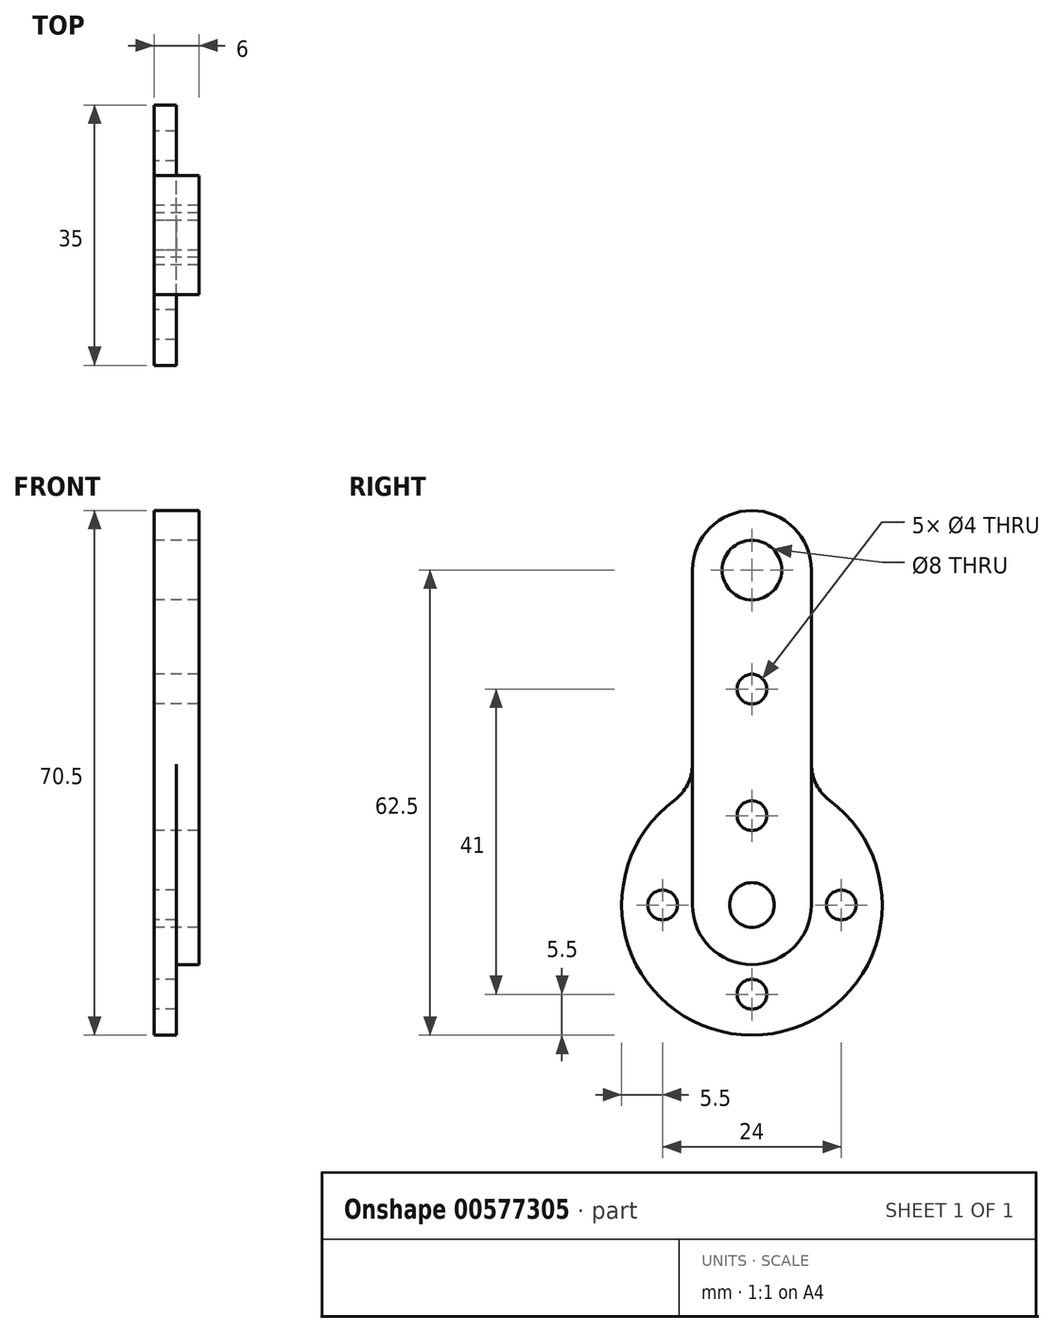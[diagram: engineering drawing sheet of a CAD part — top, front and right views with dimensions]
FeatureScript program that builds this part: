
annotation { "Feature Type Name" : "Feature", "Feature Type Description" : "" }
export const myFeature = defineFeature(function(context is Context, id is Id, definition is map)
    precondition{}
    {
        {
            var Q0;
            Q0=qCreatedBy(makeId("Right.planeOp"),FACE);
            var sketch = newSketch(context, id + "F0", { "sketchPlane" : qUnion([Q0])});
            skArc(sketch, "E0", {"start": v(-10.43, 14.06) * mm, "mid": v(0, -17.5) * mm, "end": v(10.43, 14.06) * mm});
            skCircle(sketch, "E1", {"center": v(0, 0) * mm, "radius": 3 * mm});
            skCircle(sketch, "E2", {"center": v(0, 12) * mm, "radius": 2 * mm});
            skCircle(sketch, "E3.1.0", {"center": v(-12, 0) * mm, "radius": 2 * mm});
            skCircle(sketch, "E3.2.0", {"center": v(0, -12) * mm, "radius": 2 * mm});
            skCircle(sketch, "E3.3.0", {"center": v(12, 0) * mm, "radius": 2 * mm});
            skLineSegment(sketch, "E4", {"start": v(8, 18.87) * mm, "end": v(8, 45) * mm});
            skLineSegment(sketch, "E5", {"start": v(-8, 18.87) * mm, "end": v(-8, 45) * mm});
            skArc(sketch, "E6", {"start": v(8, 45) * mm, "mid": v(0, 53) * mm, "end": v(-8, 45) * mm});
            skCircle(sketch, "E7", {"center": v(0, 45) * mm, "radius": 4 * mm});
            skPoint(sketch, "E8.visualSharp", {"position": v(-8, 15.56) * mm});
            skArc(sketch, "E8.filletArc", {"start": v(-10.43, 14.06) * mm, "mid": v(-8.64, 16.18) * mm, "end": v(-8, 18.87) * mm});
            skPoint(sketch, "E9.visualSharp", {"position": v(8, 15.56) * mm});
            skArc(sketch, "E9.filletArc", {"start": v(8, 18.87) * mm, "mid": v(8.64, 16.18) * mm, "end": v(10.43, 14.06) * mm});
            skSolve(sketch);
        }
        {
            var Q0;
            Q0 = qSketchRegion(id + "F0", true);
            extrude(context, id + "F1", {"entities" : qUnion([Q0]), "depth" : 6 * mm, "offsetDistance" : 25 * mm});
        }
        {
            var Q0;
            Q0=makeQuery(id+"F1.opExtrude","CAP_FACE",FACE,{"disambiguationData":[OSD([sQuery(id+"F0.wireOp",EDGE,"E0"),sQuery(id+"F0.wireOp",EDGE,"E1"),sQuery(id+"F0.wireOp",EDGE,"E2"),sQuery(id+"F0.wireOp",EDGE,"E3.1.0"),sQuery(id+"F0.wireOp",EDGE,"E3.2.0"),sQuery(id+"F0.wireOp",EDGE,"E3.3.0"),sQuery(id+"F0.wireOp",EDGE,"E4"),sQuery(id+"F0.wireOp",EDGE,"E5"),sQuery(id+"F0.wireOp",EDGE,"E6"),sQuery(id+"F0.wireOp",EDGE,"E7"),sQuery(id+"F0.wireOp",EDGE,"E8.filletArc"),sQuery(id+"F0.wireOp",EDGE,"E9.filletArc")])],"isStart":true});
            var sketch = newSketch(context, id + "F2", { "sketchPlane" : qUnion([Q0])});
            skCircle(sketch, "E10", {"center": v(0, 29) * mm, "radius": 2 * mm});
            skSolve(sketch);
        }
        {
            var Q0;
            Q0 = qSketchRegion(id + "F2", true);
            extrude(context, id + "F3", {"entities" : qUnion([Q0]), "operationType" : NewBodyOperationType.REMOVE, "endBound" : BoundingType.THROUGH_ALL, "oppositeDirection" : true, "depth" : 25 * mm, "offsetDistance" : 25 * mm});
        }
        {
            var Q0;
            Q0=makeQuery(id+"F1.opExtrude","CAP_FACE",FACE,{"disambiguationData":[OSD([sQuery(id+"F0.wireOp",EDGE,"E0"),sQuery(id+"F0.wireOp",EDGE,"E1"),sQuery(id+"F0.wireOp",EDGE,"E2"),sQuery(id+"F0.wireOp",EDGE,"E3.1.0"),sQuery(id+"F0.wireOp",EDGE,"E3.2.0"),sQuery(id+"F0.wireOp",EDGE,"E3.3.0"),sQuery(id+"F0.wireOp",EDGE,"E4"),sQuery(id+"F0.wireOp",EDGE,"E5"),sQuery(id+"F0.wireOp",EDGE,"E6"),sQuery(id+"F0.wireOp",EDGE,"E7"),sQuery(id+"F0.wireOp",EDGE,"E8.filletArc"),sQuery(id+"F0.wireOp",EDGE,"E9.filletArc")])],"isStart":false});
            var sketch = newSketch(context, id + "F4", { "sketchPlane" : qUnion([Q0])});
            skLineSegment(sketch, "E11", {"start": v(-8, 18.87) * mm, "end": v(-8, 0) * mm});
            skLineSegment(sketch, "E12", {"start": v(8, 18.87) * mm, "end": v(8, 0) * mm});
            skArc(sketch, "E13", {"start": v(-8, 0) * mm, "mid": v(0, -8) * mm, "end": v(8, 0) * mm});
            skArc(sketch, "E14", {"start": v(-8, 18.87) * mm, "mid": v(0, -20.5) * mm, "end": v(8, 18.87) * mm});
            skSolve(sketch);
        }
        {
            var Q0;
            Q0 = qSketchRegion(id + "F4", true);
            extrude(context, id + "F5", {"entities" : qUnion([Q0]), "operationType" : NewBodyOperationType.REMOVE, "oppositeDirection" : true, "depth" : 3 * mm, "offsetDistance" : 25.4 * mm});
        }
    });
